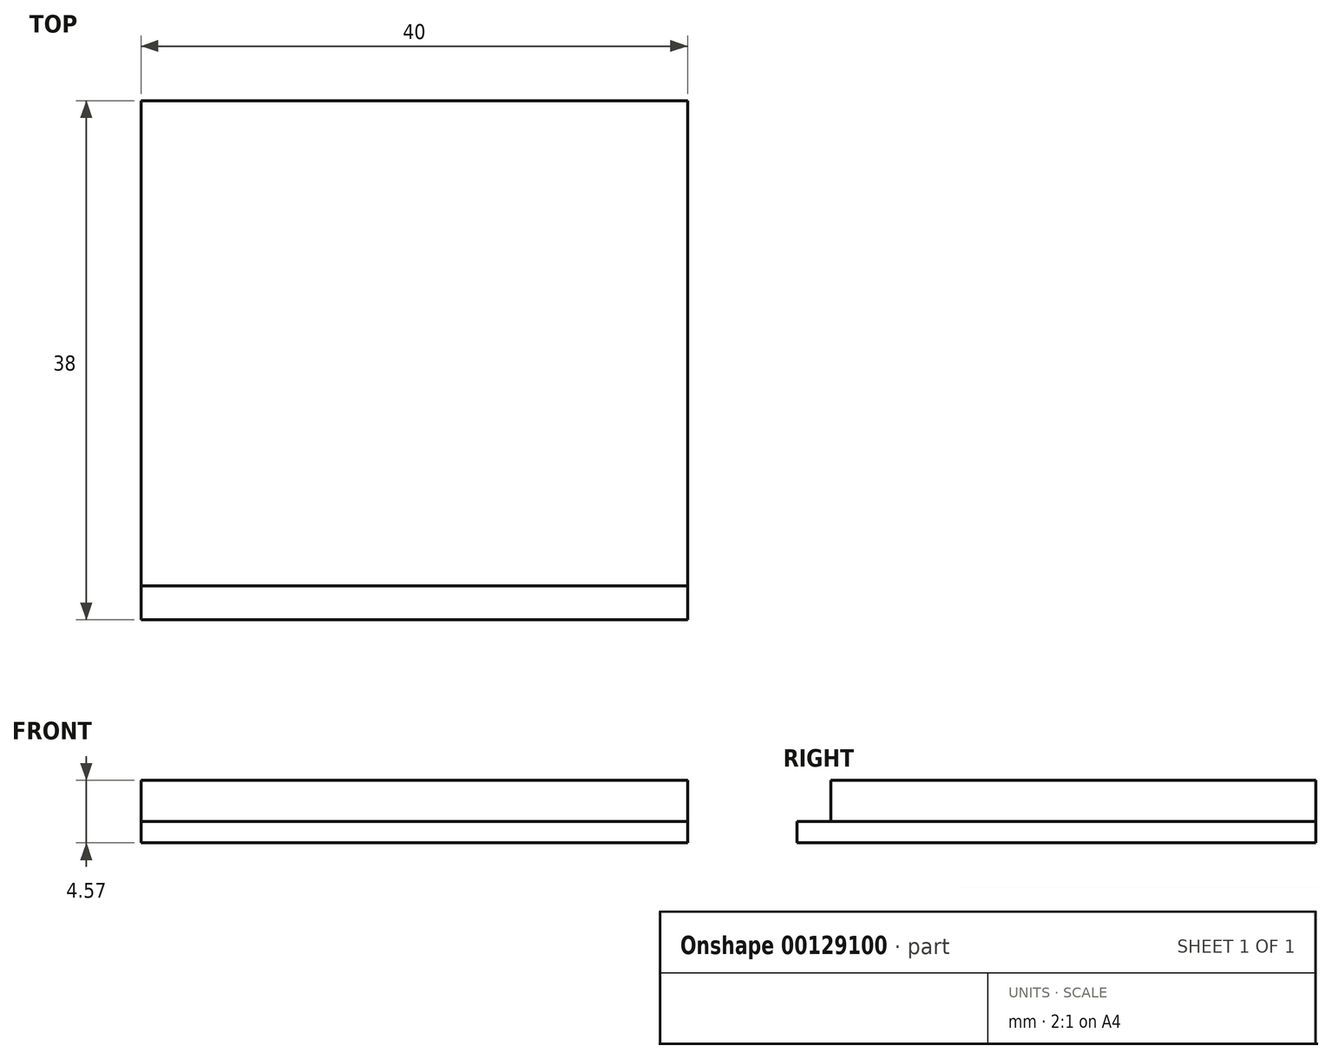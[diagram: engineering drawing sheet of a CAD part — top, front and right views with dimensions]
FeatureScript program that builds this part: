
annotation { "Feature Type Name" : "Feature", "Feature Type Description" : "" }
export const myFeature = defineFeature(function(context is Context, id is Id, definition is map)
    precondition{}
    {
        {
            var Q0;
            Q0=qCreatedBy(makeId("Top.planeOp"),FACE);
            var sketch = newSketch(context, id + "F0", { "sketchPlane" : qUnion([Q0])});
            skLineSegment(sketch, "E0.bottom", {"start": v(20, 19) * mm, "end": v(-20, 19) * mm});
            skLineSegment(sketch, "E0.top", {"start": v(20, -19) * mm, "end": v(-20, -19) * mm});
            skLineSegment(sketch, "E0.left", {"start": v(20, 19) * mm, "end": v(20, -19) * mm});
            skLineSegment(sketch, "E0.right", {"start": v(-20, 19) * mm, "end": v(-20, -19) * mm});
            skPoint(sketch, "E0.middle", {"position": v(0, 0) * mm});
            skSolve(sketch);
        }
        {
            var Q0;
            Q0 = qSketchRegion(id + "F0", true);
            extrude(context, id + "F1", {"entities" : qUnion([Q0]), "depth" : 1.57 * mm});
        }
        {
            var Q0;
            Q0=makeQuery(id+"F1.opExtrude","CAP_FACE",FACE,{"disambiguationData":[OSD([sQuery(id+"F0.wireOp",EDGE,"E0.bottom"),sQuery(id+"F0.wireOp",EDGE,"E0.top"),sQuery(id+"F0.wireOp",EDGE,"E0.left"),sQuery(id+"F0.wireOp",EDGE,"E0.right")])],"isStart":false});
            var sketch = newSketch(context, id + "F2", { "sketchPlane" : qUnion([Q0])});
            skLineSegment(sketch, "E1.bottom", {"start": v(20, 19) * mm, "end": v(-20, 19) * mm});
            skLineSegment(sketch, "E1.top", {"start": v(20, -16.5) * mm, "end": v(-20, -16.5) * mm});
            skLineSegment(sketch, "E1.left", {"start": v(20, 19) * mm, "end": v(20, -16.5) * mm});
            skLineSegment(sketch, "E1.right", {"start": v(-20, 19) * mm, "end": v(-20, -16.5) * mm});
            skSolve(sketch);
        }
        {
            var Q0;
            Q0=makeQuery(id+"F2.imprint","IMPRINT",FACE,{"disambiguationData":[TD([[makeQuery(id+"F2.imprint","IMPRINT",EDGE,{"derivedFrom":sQuery(id+"F2.wireOp",EDGE,"E1.bottom")}),1.0]])]});
            extrude(context, id + "F3", {"entities" : qUnion([Q0]), "depth" : 3 * mm});
        }
    });
